# Revit family: Shower-Shower_Door-STERLING-Vista_Pivot_II-1530D_1
name_source: partatom
category: Specialty Equipment
revit_build: Autodesk Revit 2017 (Build: 20160225_1515(x64)
units: mm (PartAtom-declared; Revit-internal decimal feet)

## family parameters
Cut with Voids When Loaded = No
Host = Face
OmniClass Number = 23.31.17.17
OmniClass Title = Shower Enclosures
Part Type = Normal
Room Calculation Point = No
Round Connector Dimension = Use Diameter
Shared = No

## types (3) — shared parameters
ADA Compliant = No
Assembly Code = C1030200
Date Modified = 07/18/2020
Default Elevation = 0"
Finish = Sterling-Metal-S-Silver
Glass Material = Sterling-Glass-G10-Pebbled_Glass_Texture
Height = 69"
Length = 2 1/8"
Manufacturer = STERLING Co.
Maste Format 2014 = 10 28 19.16
Master Format 2014 Name = Shower Door
Material = Anodized Aluminum
Product Documentation Link = https://resources.kohler.com
Product Name = Vista Pivot II
Product Page URL = http://www.sterlingplumbing.com
URL = https://www.sterlingplumbing.com
https://www.sterlingplumbing.com
WaterSense Certified = No

## per-type parameters (varying)
| type | Description | Model | Panel Offset | Type |
| 36 Inch Width,Pebbled Glass Texture,S-Silver Frame | Framed pivot shower door, 69inch H x 31-1/4 - 36 inch W, with 1/8 inch thick Pebbled glass | 1530D-36S | 4 3/8" | 1 |
| 42 Inch Width, Pebbled Glass Texture,S-Silver Frame | Framed pivot shower door, 69inch H x 36 - 42inch W, with 1/8inch thick Pebbled glass | 1530D-42S | 5" | 2 |
| 48 Inch Width, Pebbled Glass Texture, S-Silver Frame | Framed pivot shower door, 69inch H x 42 - 48inch W, with 1/8inch thick Pebbled glass | 1530D-48S | 5" | 3 |

## geometry (parser evidence)
native form markers: Sweep x4
no freeform markers — native parametric forms only
